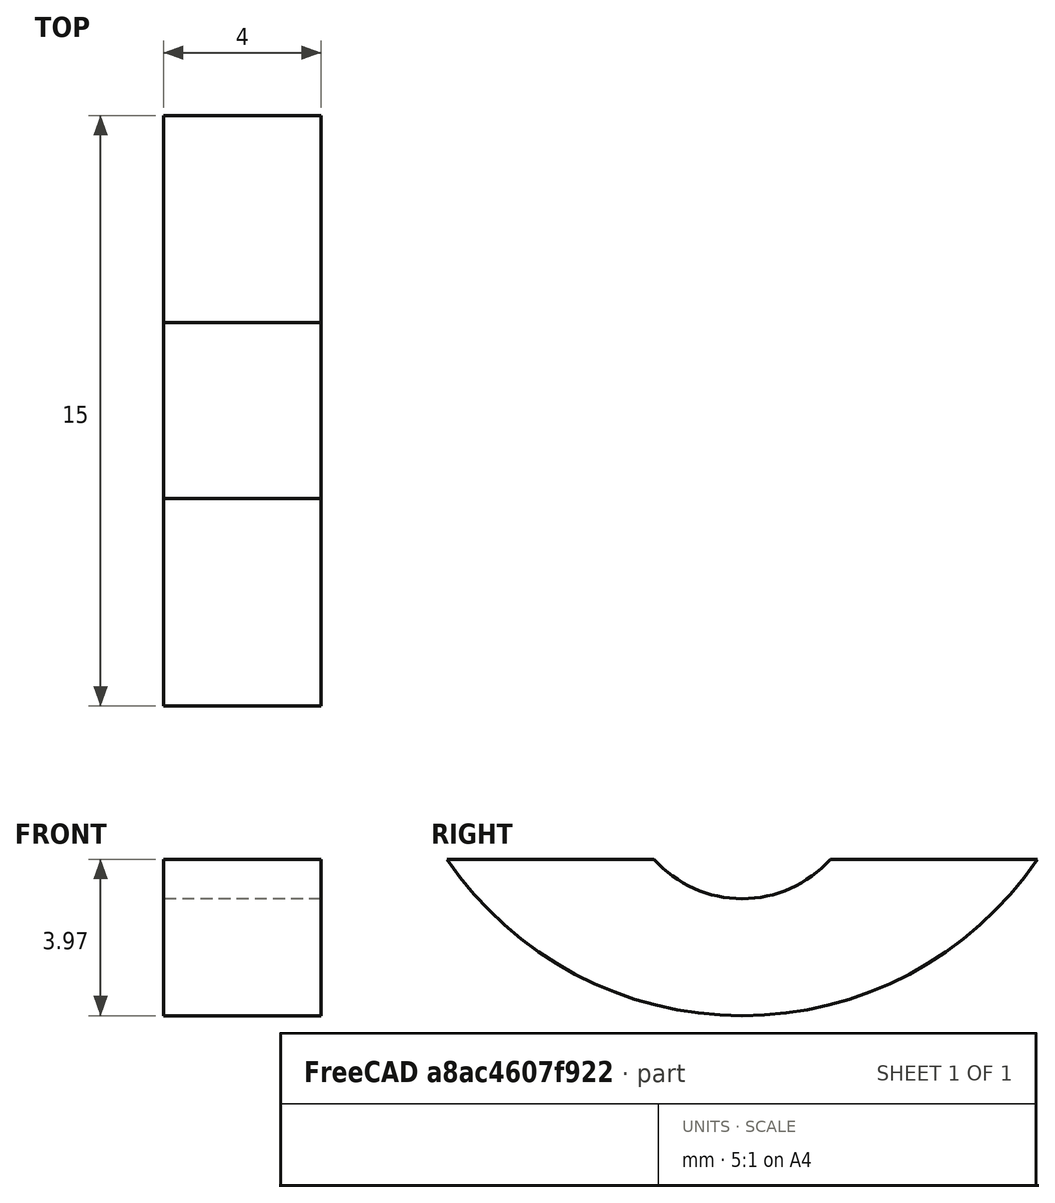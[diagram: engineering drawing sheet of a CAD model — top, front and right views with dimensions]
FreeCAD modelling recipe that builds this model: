
FCSTD DOCUMENT  (FreeCAD 0.21R33771 (Git))
Label: FRAME_MOTOR_SUPPORT
License: All rights reserved
LicenseURL: http://en.wikipedia.org/wiki/All_rights_reserved
objects: Sketcher::SketchObject×2, PartDesign::Pad×1, PartDesign::Body×1
note: 5 computed .brp shape members not serialized (recipe doc carries the construction recipe); baked Part::Feature solids carry a one-line shape summary decoded from their .brp

FEATURE [Sketcher::SketchObject] Sketch
  FullyConstrained = false
  MapMode = 5
  Placement = pos=(0,0,0) rot=(0.57735,0.57735,0.57735;2.0944rad)
  Support = -> [YZ_Plane]
  sketch-geometry (7):
    g0: Circle CenterX=0 CenterY=0 CenterZ=0 NormalX=0 NormalY=0 NormalZ=1 AngleXU=0 Radius=3
    g1: Circle CenterX=0 CenterY=0 CenterZ=0 NormalX=0 NormalY=0 NormalZ=1 AngleXU=0 Radius=5
    g2: LineSegment StartX=-8.17669 StartY=2 StartZ=0 EndX=-8.17669 EndY=-2 EndZ=0
    g3: LineSegment StartX=-8.17669 StartY=-2 StartZ=0 EndX=8.17669 EndY=-2 EndZ=0
    g4: LineSegment StartX=8.17669 StartY=-2 StartZ=0 EndX=8.17669 EndY=2 EndZ=0
    g5: LineSegment StartX=8.17669 StartY=2 StartZ=0 EndX=-8.17669 EndY=2 EndZ=0
    g6: GeomPoint X=0 Y=0 Z=0
  constraints (15):
    c: Coincident(g0,g-1)
    c: Coincident(g1,g0)
    c: Diameter(g0) = 6
    c: Diameter(g1) = 10
    c: Coincident(g2,g3)
    c: Coincident(g3,g4)
    c: Coincident(g4,g5)
    c: Coincident(g5,g2)
    c: Horizontal(g3)
    c: Horizontal(g5)
    c: Vertical(g2)
    c: Vertical(g4)
    c: Symmetric(g3,g2,g6)
    c: Coincident(g6,g0)
    c: DistanceY(g4,g4) = 4
FEATURE [Sketcher::SketchObject] Sketch001
  ExternalGeometry = -> [Sketch]
  FullyConstrained = false
  MapMode = 5
  Placement = pos=(0,0,0) rot=(0.57735,0.57735,0.57735;2.0944rad)
  Support = -> [YZ_Plane]
  sketch-geometry (6):
    g0: GeomPoint X=-2.23607 Y=-2 Z=0
    g1: GeomPoint X=2.23607 Y=-2 Z=0
    g2: ArcOfCircle CenterX=2e-16 CenterY=8e-16 CenterZ=0 NormalX=0 NormalY=0 NormalZ=1 AngleXU=0 Radius=3 StartAngle=3.87132 EndAngle=5.55346
    g3: LineSegment StartX=-2.23607 StartY=-2 StartZ=0 EndX=-7.49928 EndY=-2 EndZ=0
    g4: LineSegment StartX=2.23607 StartY=-2 StartZ=0 EndX=7.49928 EndY=-2 EndZ=0
    g5: ArcOfCircle CenterX=5e-16 CenterY=3.09415 CenterZ=0 NormalX=0 NormalY=0 NormalZ=1 AngleXU=0 Radius=9.06585 StartAngle=3.73828 EndAngle=5.6865
  constraints (14):
    c: PointOnObject(g0,g-4)
    c: PointOnObject(g0,g-3)
    c: PointOnObject(g1,g-4)
    c: PointOnObject(g1,g-3)
    c: Coincident(g2,g0)
    c: Coincident(g2,g1)
    c: Tangent(g2,g-4)
    c: Coincident(g3,g2)
    c: Horizontal(g3)
    c: Coincident(g4,g2)
    c: Horizontal(g4)
    c: Coincident(g5,g3)
    c: Coincident(g5,g4)
    c: Equal(g4,g3)
FEATURE [PartDesign::Pad] Pad
  Direction = (1,-2e-16,3e-16)
  Length = 4
  Length2 = 10
  Placement = pos=(0,0,0) rot=(1,1,1;2.0944rad)
  Profile = -> Sketch001
  ReferenceAxis = -> Sketch001 [N_Axis]
  Type = 0
FEATURE [PartDesign::Body] Body
  Group = -> [Sketch,Sketch001,Pad]
  Origin = -> Origin
  Tip = -> Pad
